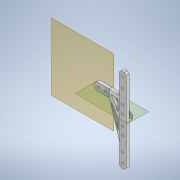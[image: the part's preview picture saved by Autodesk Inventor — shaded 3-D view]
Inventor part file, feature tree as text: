
AUTODESK INVENTOR PART (.ipt)
format: ipt  version: 2020 (Build 240168000, 168)  size: 307,200 bytes
history: native  units: mm
features: other x8, projected_geometry x7, sketch x6, extrude x5, fillet x4, plane x3, reference x3, chamfer x2, loft x1
ambient origin geometry x8: Origin, YZ Plane, XZ Plane, XY Plane, X Axis, Y Axis, Z Axis, Center Point
bodies: Solid1 (feature_tree)
feature tree (39):
  extrude  "Extrusion1"  Depth=87.0mm
  plane  "Work Plane1"
  plane  "Work Plane2"
  extrude  "Extrusion2"  Depth=2.0mm
  sketch  "Sketch3"  dims[d4=2.0mm d5=2.0mm]
  loft  "Loft1"
  plane  "Work Plane3"
  extrude  "Extrusion3"  Depth=8.0mm
  fillet  "Fillet1"  Radius=15.0mm
  extrude  "Extrusion4"  Depth=2.0mm
  fillet  "Fillet2"  Radius=3.0mm
  fillet  "Fillet3"  Radius=3.0mm
  chamfer  "Chamfer1"  Distance=3.0mm
  chamfer  "Chamfer2"  Distance=20.0mm
  extrude  "Extrusion5"  TaperAngle=0.0deg  [1 undecoded]
  fillet  "Fillet4"  [1 undecoded]
  sketch  "Sketch1"  dims[d0=7.0mm d1=87.0mm]
  reference  "Reference1"
  reference  "Reference2"
  sketch  "Sketch2"  dims[d2=2.0mm d3=2.0mm]
  reference  "Reference3"
  projected_geometry  "Projected Loop1"
  other  "Edges1"
  sketch  "Sketch5"  dims[d6=3.0mm d7=0.0mm d8=8.0mm d9=15.0mm]
  projected_geometry  "Projected Loop3"
  projected_geometry  "Projected Loop4"
  sketch  "Sketch6"  dims[d10=2.0mm d11=2.0mm d12=3.0mm d13=0.0mm d14=3.0mm]
  projected_geometry  "Projected Loop5"
  projected_geometry  "Projected Loop6"
  sketch  "Sketch7"  dims[d15=20.0mm d16=3.0mm d17=20.0mm d18=0.0mm d19=90.0deg d20=0.0mm d21=90.0deg d22=5.0mm d23=2.0mm d24=0.0mm d25=3.0mm d26=2.0mm d27=2.0mm d28=4.0mm d29=4.0mm d30=2.0mm d31=2.0mm d32=3.0mm d33=0.0mm d34=0.5mm d35=1.0mm d36=1.5mm d37=3.0mm d38=2.0mm d39=2.0mm d40=45.0deg d41=2.0mm d42=2.0mm d43=45.0deg d44=15.0mm d45=8.0mm d46=15.0mm d47=8.0mm d48=2.0mm d49=2.0mm d50=2.0mm d51=2.0mm d52=3.0mm d53=0.0mm d54=1.0mm]
  projected_geometry  "Projected Loop7"
  projected_geometry  "Projected Loop8"
  parser-record x1  (decoder bookkeeping rows leaked as tree rows — omitted from the tree; the rows remain in map.json)
  other  "body_8d_1.iam"
  other  "leg_2d_1:2"
  other  "leg_holder_2:1"
  other  "leg_1_2d_MIR:2"
  other  "leg_holder_2_MIR:1"
  other  "body_linker_1_8d:1"
note: 2 required parameter values undecoded (feature->parameter linkage not recoverable at this tier; creation-order binding heuristic only, values carry confidence <= 0.55)
note: 1 file-system path scrubbed to <path> (originals preserved in map.json)
